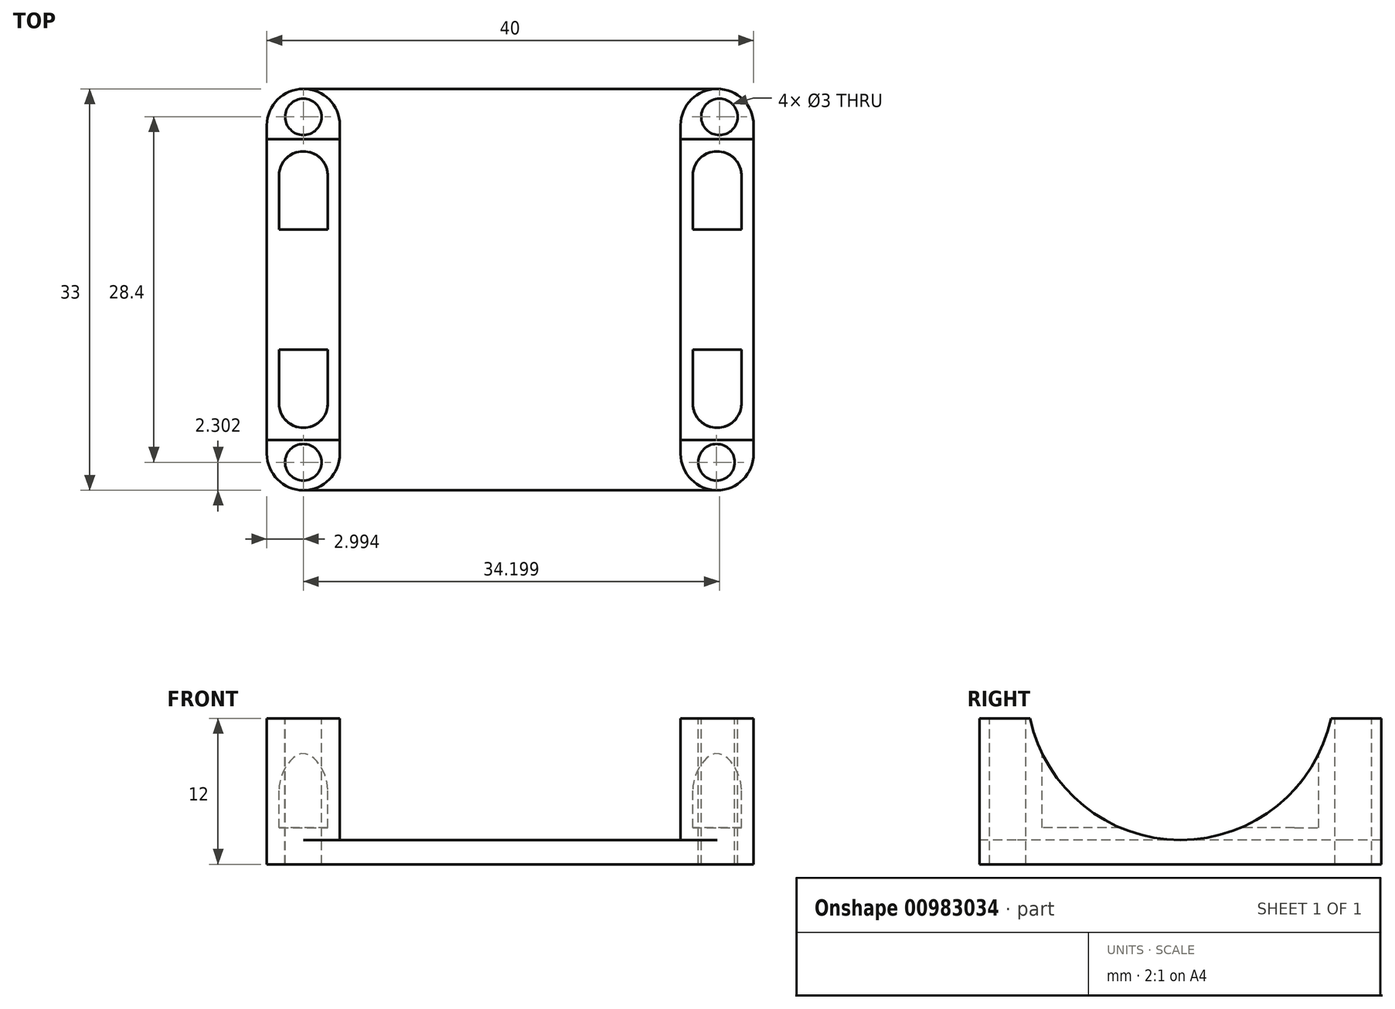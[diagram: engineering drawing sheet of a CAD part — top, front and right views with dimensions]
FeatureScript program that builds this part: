
annotation { "Feature Type Name" : "Feature", "Feature Type Description" : "" }
export const myFeature = defineFeature(function(context is Context, id is Id, definition is map)
    precondition{}
    {
        {
            var Q0;
            Q0=qCreatedBy(makeId("Top.planeOp"),FACE);
            var sketch = newSketch(context, id + "F0", { "sketchPlane" : qUnion([Q0])});
            skLineSegment(sketch, "E0.bottom", {"start": v(-28.73, 14.81) * mm, "end": v(11.27, 14.81) * mm});
            skLineSegment(sketch, "E0.top", {"start": v(-28.73, -18.19) * mm, "end": v(11.27, -18.19) * mm});
            skLineSegment(sketch, "E0.left", {"start": v(-28.73, 14.81) * mm, "end": v(-28.73, -18.19) * mm});
            skLineSegment(sketch, "E0.right", {"start": v(11.27, 14.81) * mm, "end": v(11.27, -18.19) * mm});
            skSolve(sketch);
        }
        {
            var Q0;
            Q0 = qSketchRegion(id + "F0", true);
            extrude(context, id + "F1", {"entities" : qUnion([Q0]), "depth" : 12 * mm, "offsetDistance" : 25 * mm});
        }
        {
            var Q0;
            Q0=makeQuery(id+"F1.opExtrude","SWEPT_FACE",FACE,{"disambiguationData":[OSD([sQuery(id+"F0.wireOp",EDGE,"E0.right")])]});
            var sketch = newSketch(context, id + "F2", { "sketchPlane" : qUnion([Q0])});
            skCircle(sketch, "E1", {"center": v(-1.69, 14.65) * mm, "radius": 12.65 * mm});
            skPoint(sketch, "E1.centerSnap0", {"position": v(-1.69, 12) * mm});
            skSolve(sketch);
        }
        {
            var Q0;
            Q0 = qSketchRegion(id + "F2", true);
            extrude(context, id + "F3", {"entities" : qUnion([Q0]), "operationType" : NewBodyOperationType.REMOVE, "oppositeDirection" : true, "depth" : 69 * mm, "offsetDistance" : 25 * mm});
        }
        {
            var Q0;
            {var subQ0=sQuery(id+"F0.wireOp",EDGE,"E0.top");var subQ1=sQuery(id+"F0.wireOp",EDGE,"E0.left");var subQ2=sQuery(id+"F0.wireOp",EDGE,"E0.right");Q0=makeQuery(id+"F3.boolean.opBoolean","SPLIT",FACE,{"disambiguationData":[TD([makeQuery(id+"F1.opExtrude","SWEPT_FACE",FACE,{"disambiguationData":[OSD([subQ0])]})])],"derivedFrom":makeQuery(id+"F1.opExtrude","CAP_FACE",FACE,{"disambiguationData":[OSD([sQuery(id+"F0.wireOp",EDGE,"E0.bottom"),subQ0,subQ1,subQ2])],"isStart":false})});}
            var sketch = newSketch(context, id + "F4", { "sketchPlane" : qUnion([Q0])});
            skLineSegment(sketch, "E2.bottom", {"start": v(5.27, 29.68) * mm, "end": v(-22.73, 29.68) * mm});
            skLineSegment(sketch, "E2.top", {"start": v(5.27, -19.11) * mm, "end": v(-22.73, -19.11) * mm});
            skLineSegment(sketch, "E2.left", {"start": v(5.27, 29.68) * mm, "end": v(5.27, -19.11) * mm});
            skLineSegment(sketch, "E2.right", {"start": v(-22.73, 29.68) * mm, "end": v(-22.73, -19.11) * mm});
            skSolve(sketch);
        }
        {
            var Q0;
            Q0 = qSketchRegion(id + "F4", true);
            extrude(context, id + "F5", {"entities" : qUnion([Q0]), "operationType" : NewBodyOperationType.REMOVE, "oppositeDirection" : true, "depth" : 10 * mm, "offsetDistance" : 25 * mm});
        }
        {
            var Q0;
            {var subQ0=sQuery(id+"F0.wireOp",EDGE,"E0.bottom");var subQ1=makeQuery(id+"F1.opExtrude","SWEPT_FACE",FACE,{"disambiguationData":[OSD([subQ0])]});var subQ2=sQuery(id+"F0.wireOp",EDGE,"E0.left");var subQ3=makeQuery(id+"F1.opExtrude","SWEPT_FACE",FACE,{"disambiguationData":[OSD([subQ2])]});var subQ5=sQuery(id+"F0.wireOp",EDGE,"E0.right");Q0=makeQuery(id+"F5.boolean.opBoolean","SPLIT",FACE,{"disambiguationData":[TD([subQ3])],"derivedFrom":makeQuery(id+"F3.boolean.opBoolean","SPLIT",FACE,{"disambiguationData":[TD([subQ1])],"derivedFrom":makeQuery(id+"F1.opExtrude","CAP_FACE",FACE,{"disambiguationData":[OSD([subQ0,sQuery(id+"F0.wireOp",EDGE,"E0.top"),subQ2,subQ5])],"isStart":false})})});}
            var sketch = newSketch(context, id + "F6", { "sketchPlane" : qUnion([Q0])});
            skLineSegment(sketch, "E3.bottom", {"start": v(-25.73, 9.68) * mm, "end": v(-25.73, 9.68) * mm});
            skLineSegment(sketch, "E3.top", {"start": v(-25.73, -13.06) * mm, "end": v(-25.73, -13.06) * mm});
            skLineSegment(sketch, "E3.left", {"start": v(-27.73, 7.68) * mm, "end": v(-27.73, -11.06) * mm});
            skLineSegment(sketch, "E3.right", {"start": v(-23.73, 7.68) * mm, "end": v(-23.73, -11.06) * mm});
            skLineSegment(sketch, "E4.bottom", {"start": v(8.27, 9.68) * mm, "end": v(8.27, 9.68) * mm});
            skLineSegment(sketch, "E4.top", {"start": v(8.27, -13.06) * mm, "end": v(8.27, -13.06) * mm});
            skLineSegment(sketch, "E4.left", {"start": v(6.27, 7.68) * mm, "end": v(6.27, -11.06) * mm});
            skLineSegment(sketch, "E4.right", {"start": v(10.27, 7.68) * mm, "end": v(10.27, -11.06) * mm});
            skPoint(sketch, "E5.visualSharp", {"position": v(-27.73, 9.68) * mm});
            skArc(sketch, "E5.filletArc", {"start": v(-25.73, 9.68) * mm, "mid": v(-27.14, 9.1) * mm, "end": v(-27.73, 7.68) * mm});
            skPoint(sketch, "E6.visualSharp", {"position": v(-27.73, -13.06) * mm});
            skArc(sketch, "E6.filletArc", {"start": v(-27.73, -11.06) * mm, "mid": v(-27.14, -12.47) * mm, "end": v(-25.73, -13.06) * mm});
            skPoint(sketch, "E7.visualSharp", {"position": v(-23.73, -13.06) * mm});
            skArc(sketch, "E7.filletArc", {"start": v(-25.73, -13.06) * mm, "mid": v(-24.31, -12.47) * mm, "end": v(-23.73, -11.06) * mm});
            skPoint(sketch, "E8.visualSharp", {"position": v(-23.73, 9.68) * mm});
            skArc(sketch, "E8.filletArc", {"start": v(-23.73, 7.68) * mm, "mid": v(-24.31, 9.1) * mm, "end": v(-25.73, 9.68) * mm});
            skPoint(sketch, "E9.visualSharp", {"position": v(6.27, 9.68) * mm});
            skArc(sketch, "E9.filletArc", {"start": v(8.27, 9.68) * mm, "mid": v(6.86, 9.1) * mm, "end": v(6.27, 7.68) * mm});
            skPoint(sketch, "E10.visualSharp", {"position": v(6.27, -13.06) * mm});
            skArc(sketch, "E10.filletArc", {"start": v(6.27, -11.06) * mm, "mid": v(6.86, -12.47) * mm, "end": v(8.27, -13.06) * mm});
            skPoint(sketch, "E11.visualSharp", {"position": v(10.27, -13.06) * mm});
            skArc(sketch, "E11.filletArc", {"start": v(8.27, -13.06) * mm, "mid": v(9.69, -12.47) * mm, "end": v(10.27, -11.06) * mm});
            skPoint(sketch, "E12.visualSharp", {"position": v(10.27, 9.68) * mm});
            skArc(sketch, "E12.filletArc", {"start": v(10.27, 7.68) * mm, "mid": v(9.69, 9.1) * mm, "end": v(8.27, 9.68) * mm});
            skSolve(sketch);
        }
        {
            var Q0;
            Q0=makeQuery(id+"F6.imprint","IMPRINT",FACE,{"disambiguationData":[TD([[makeQuery(id+"F6.imprint","IMPRINT",EDGE,{"derivedFrom":sQuery(id+"F6.wireOp",EDGE,"E3.left")}),1.0]])]});
            var Q1;
            Q1=makeQuery(id+"F6.imprint","IMPRINT",FACE,{"disambiguationData":[TD([[makeQuery(id+"F6.imprint","IMPRINT",EDGE,{"derivedFrom":sQuery(id+"F6.wireOp",EDGE,"E4.left")}),1.0]])]});
            extrude(context, id + "F7", {"entities" : qUnion([Q0, Q1]), "operationType" : NewBodyOperationType.REMOVE, "oppositeDirection" : true, "depth" : 9 * mm, "offsetDistance" : 25 * mm});
        }
        {
            var Q0;
            Q0=makeQuery(id+"F5.boolean.opBoolean","INTERSECT",EDGE,{"derivedFrom":[makeQuery(id+"F1.opExtrude","SWEPT_FACE",FACE,{"disambiguationData":[OSD([sQuery(id+"F0.wireOp",EDGE,"E0.bottom")])]}),makeQuery(id+"F5.opExtrude","SWEPT_FACE",FACE,{"disambiguationData":[OSD([sQuery(id+"F4.wireOp",EDGE,"E2.left")])]})]});
            var Q1;
            Q1=makeQuery(id+"F1.opExtrude","SWEPT_EDGE",EDGE,{"disambiguationData":[OSD([sQuery(id+"F0.wireOp",EDGE,"E0.bottom"),sQuery(id+"F0.wireOp",EDGE,"E0.right")])]});
            var Q2;
            Q2=makeQuery(id+"F5.boolean.opBoolean","INTERSECT",EDGE,{"derivedFrom":[makeQuery(id+"F1.opExtrude","SWEPT_FACE",FACE,{"disambiguationData":[OSD([sQuery(id+"F0.wireOp",EDGE,"E0.bottom")])]}),makeQuery(id+"F5.opExtrude","SWEPT_FACE",FACE,{"disambiguationData":[OSD([sQuery(id+"F4.wireOp",EDGE,"E2.right")])]})]});
            var Q3;
            Q3=makeQuery(id+"F1.opExtrude","SWEPT_EDGE",EDGE,{"disambiguationData":[OSD([sQuery(id+"F0.wireOp",EDGE,"E0.bottom"),sQuery(id+"F0.wireOp",EDGE,"E0.left")])]});
            var Q4;
            Q4=makeQuery(id+"F1.opExtrude","SWEPT_EDGE",EDGE,{"disambiguationData":[OSD([sQuery(id+"F0.wireOp",EDGE,"E0.top"),sQuery(id+"F0.wireOp",EDGE,"E0.left")])]});
            var Q5;
            Q5=makeQuery(id+"F5.boolean.opBoolean","INTERSECT",EDGE,{"derivedFrom":[makeQuery(id+"F1.opExtrude","SWEPT_FACE",FACE,{"disambiguationData":[OSD([sQuery(id+"F0.wireOp",EDGE,"E0.top")])]}),makeQuery(id+"F5.opExtrude","SWEPT_FACE",FACE,{"disambiguationData":[OSD([sQuery(id+"F4.wireOp",EDGE,"E2.right")])]})]});
            var Q6;
            Q6=makeQuery(id+"F5.boolean.opBoolean","INTERSECT",EDGE,{"derivedFrom":[makeQuery(id+"F1.opExtrude","SWEPT_FACE",FACE,{"disambiguationData":[OSD([sQuery(id+"F0.wireOp",EDGE,"E0.top")])]}),makeQuery(id+"F5.opExtrude","SWEPT_FACE",FACE,{"disambiguationData":[OSD([sQuery(id+"F4.wireOp",EDGE,"E2.left")])]})]});
            var Q7;
            Q7=makeQuery(id+"F1.opExtrude","SWEPT_EDGE",EDGE,{"disambiguationData":[OSD([sQuery(id+"F0.wireOp",EDGE,"E0.top"),sQuery(id+"F0.wireOp",EDGE,"E0.right")])]});
            fillet(context, id + "F8", {"entities" : qUnion([Q0, Q1, Q2, Q3, Q4, Q5, Q6, Q7]), "radius" : 3 * mm, "tangentPropagation" : true, "allowEdgeOverflow" : false});
        }
        {
            var Q0;
            {var subQ0=sQuery(id+"F0.wireOp",EDGE,"E0.bottom");var subQ1=makeQuery(id+"F1.opExtrude","SWEPT_FACE",FACE,{"disambiguationData":[OSD([subQ0])]});var subQ2=sQuery(id+"F0.wireOp",EDGE,"E0.left");var subQ3=makeQuery(id+"F1.opExtrude","SWEPT_FACE",FACE,{"disambiguationData":[OSD([subQ2])]});var subQ5=sQuery(id+"F0.wireOp",EDGE,"E0.right");Q0=makeQuery(id+"F5.boolean.opBoolean","SPLIT",FACE,{"disambiguationData":[TD([subQ3])],"derivedFrom":makeQuery(id+"F3.boolean.opBoolean","SPLIT",FACE,{"disambiguationData":[TD([subQ1])],"derivedFrom":makeQuery(id+"F1.opExtrude","CAP_FACE",FACE,{"disambiguationData":[OSD([subQ0,sQuery(id+"F0.wireOp",EDGE,"E0.top"),subQ2,subQ5])],"isStart":false})})});}
            var sketch = newSketch(context, id + "F9", { "sketchPlane" : qUnion([Q0])});
            skCircle(sketch, "E13", {"center": v(-25.73, 12.51) * mm, "radius": 1.5 * mm});
            skPoint(sketch, "E13.centerSnap0", {"position": v(-25.73, 14.81) * mm});
            skCircle(sketch, "E14", {"center": v(8.46, 12.51) * mm, "radius": 1.5 * mm});
            skCircle(sketch, "E15", {"center": v(8.22, -15.89) * mm, "radius": 1.5 * mm});
            skCircle(sketch, "E16", {"center": v(-25.74, -15.89) * mm, "radius": 1.5 * mm});
            skSolve(sketch);
        }
        {
            var Q0;
            Q0 = qSketchRegion(id + "F9", true);
            extrude(context, id + "F10", {"entities" : qUnion([Q0]), "operationType" : NewBodyOperationType.REMOVE, "oppositeDirection" : true, "depth" : 20 * mm, "offsetDistance" : 25 * mm});
        }
    });
